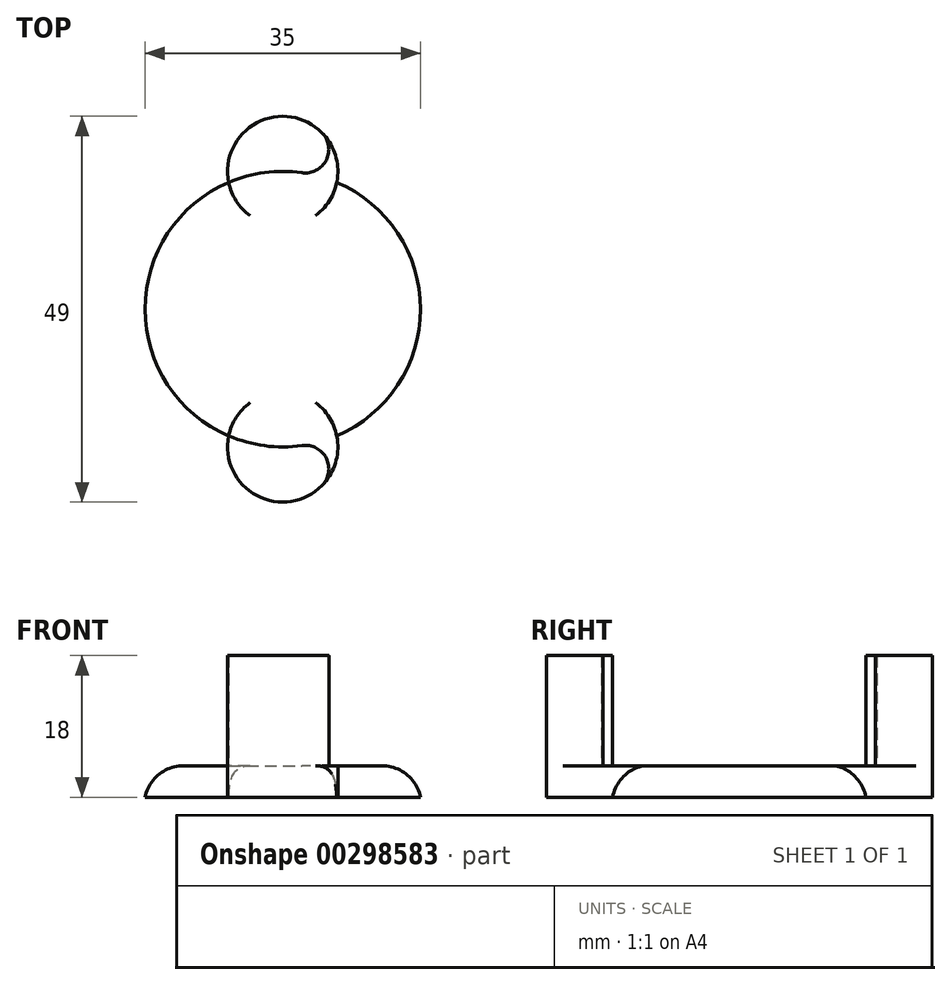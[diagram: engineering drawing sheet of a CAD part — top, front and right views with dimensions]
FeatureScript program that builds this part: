
annotation { "Feature Type Name" : "Feature", "Feature Type Description" : "" }
export const myFeature = defineFeature(function(context is Context, id is Id, definition is map)
    precondition{}
    {
        {
            var Q0;
            Q0=qCreatedBy(makeId("Top.planeOp"),FACE);
            var sketch = newSketch(context, id + "F0", { "sketchPlane" : qUnion([Q0])});
            skCircle(sketch, "E0", {"center": v(0, 0) * mm, "radius": 17.5 * mm});
            skSolve(sketch);
        }
        {
            var Q0;
            Q0 = qSketchRegion(id + "F0", true);
            extrude(context, id + "F1", {"entities" : qUnion([Q0]), "endBound" : BoundingType.SYMMETRIC, "depth" : 4 * mm});
        }
        {
            var Q0;
            Q0=makeQuery(id+"F1.opExtrude","CAP_FACE",FACE,{"disambiguationData":[OSD([sQuery(id+"F0.wireOp",EDGE,"E0")])],"isStart":true});
            var sketch = newSketch(context, id + "F2", { "sketchPlane" : qUnion([Q0])});
            skCircle(sketch, "E1.0.0", {"center": v(0, 0) * mm, "radius": 17.5 * mm});
            skArc(sketch, "E2", {"start": v(-6.86, -16.1) * mm, "mid": v(0, -24.5) * mm, "end": v(6.86, -16.1) * mm});
            skArc(sketch, "E3", {"start": v(6.86, 16.1) * mm, "mid": v(0, 24.5) * mm, "end": v(-6.86, 16.1) * mm});
            skSolve(sketch);
        }
        {
            var Q0;
            {var subQ0=sQuery(id+"F2.wireOp",EDGE,"E3");Q0=makeQuery(id+"F2.imprint","IMPRINT",FACE,{"disambiguationData":[TD([[makeQuery(id+"F2.imprint","IMPRINT",EDGE,{"derivedFrom":subQ0}),1.0]])]});}
            var Q1;
            {var subQ0=sQuery(id+"F2.wireOp",EDGE,"E2");Q1=makeQuery(id+"F2.imprint","IMPRINT",FACE,{"disambiguationData":[TD([[makeQuery(id+"F2.imprint","IMPRINT",EDGE,{"derivedFrom":subQ0}),1.0]])]});}
            extrude(context, id + "F3", {"entities" : qUnion([Q0, Q1]), "operationType" : NewBodyOperationType.ADD, "oppositeDirection" : true, "depth" : 18 * mm});
        }
        {
            var Q0;
            {var subQ0=sQuery(id+"F0.wireOp",EDGE,"E0");var subQ1=sQuery(id+"F2.wireOp",EDGE,"E3");var subQ2=sQuery(id+"F2.wireOp",EDGE,"E1.0.0");Q0=makeQuery(id+"F3.boolean.opBoolean","SPLIT",EDGE,{"disambiguationData":[topologyDisambiguationEdgeConnected([makeQuery(id+"F1.opExtrude","CAP_FACE",FACE,{"disambiguationData":[OSD([subQ0])],"isStart":false}),makeQuery(id+"F3.opExtrude","SWEPT_FACE",FACE,{"disambiguationData":[OSD([subQ2]),TDD([makeQuery(id+"F2.imprint","IMPRINT",EDGE,{"disambiguationData":[TD([[makeQuery(id+"F2.imprint","INTERSECT",VERTEX,{"disambiguationData":[OD(0.0)],"derivedFrom":[subQ2,subQ1]}),1.0]])],"derivedFrom":subQ2})])]})])],"derivedFrom":makeQuery(id+"F1.opExtrude","CAP_EDGE",EDGE,{"disambiguationData":[OSD([subQ0])],"isStart":false})});}
            var Q1;
            {var subQ0=sQuery(id+"F0.wireOp",EDGE,"E0");var subQ1=sQuery(id+"F2.wireOp",EDGE,"E2");var subQ2=sQuery(id+"F2.wireOp",EDGE,"E1.0.0");Q1=makeQuery(id+"F3.boolean.opBoolean","SPLIT",EDGE,{"disambiguationData":[topologyDisambiguationEdgeConnected([makeQuery(id+"F1.opExtrude","CAP_FACE",FACE,{"disambiguationData":[OSD([subQ0])],"isStart":false}),makeQuery(id+"F3.opExtrude","SWEPT_FACE",FACE,{"disambiguationData":[OSD([subQ2]),TDD([makeQuery(id+"F2.imprint","IMPRINT",EDGE,{"disambiguationData":[TD([[makeQuery(id+"F2.imprint","INTERSECT",VERTEX,{"disambiguationData":[OD(0.0)],"derivedFrom":[subQ2,subQ1]}),1.0]])],"derivedFrom":subQ2})])]})])],"derivedFrom":makeQuery(id+"F1.opExtrude","CAP_EDGE",EDGE,{"disambiguationData":[OSD([subQ0])],"isStart":false})});}
            fillet(context, id + "F4", {"entities" : qUnion([Q0, Q1]), "radius" : 5 * mm, "tangentPropagation" : true, "allowEdgeOverflow" : false});
        }
        {
            var Q0;
            {var subQ0=sQuery(id+"F2.wireOp",EDGE,"E3");var subQ1=sQuery(id+"F2.wireOp",EDGE,"E1.0.0");Q0=makeQuery(id+"F3.boolean.opBoolean","SPLIT",EDGE,{"disambiguationData":[topologyDisambiguationEdgeConnected([makeQuery(id+"F1.opExtrude","SWEPT_FACE",FACE,{"disambiguationData":[OSD([sQuery(id+"F0.wireOp",EDGE,"E0")])]})])],"derivedFrom":makeQuery(id+"F3.opExtrude","SWEPT_EDGE",EDGE,{"disambiguationData":[OSD([subQ1,subQ0]),TDD([makeQuery(id+"F2.imprint","INTERSECT",VERTEX,{"disambiguationData":[OD(0.0)],"derivedFrom":[subQ1,subQ0]})])]})});}
            var Q1;
            {var subQ0=sQuery(id+"F2.wireOp",EDGE,"E2");var subQ1=sQuery(id+"F2.wireOp",EDGE,"E1.0.0");Q1=makeQuery(id+"F3.boolean.opBoolean","SPLIT",EDGE,{"disambiguationData":[topologyDisambiguationEdgeConnected([makeQuery(id+"F1.opExtrude","SWEPT_FACE",FACE,{"disambiguationData":[OSD([sQuery(id+"F0.wireOp",EDGE,"E0")])]})])],"derivedFrom":makeQuery(id+"F3.opExtrude","SWEPT_EDGE",EDGE,{"disambiguationData":[OSD([subQ1,subQ0]),TDD([makeQuery(id+"F2.imprint","INTERSECT",VERTEX,{"disambiguationData":[OD(1.0)],"derivedFrom":[subQ1,subQ0]})])]})});}
            var Q2;
            {var subQ0=sQuery(id+"F2.wireOp",EDGE,"E2");var subQ1=sQuery(id+"F2.wireOp",EDGE,"E1.0.0");Q2=makeQuery(id+"F3.boolean.opBoolean","SPLIT",EDGE,{"disambiguationData":[topologyDisambiguationEdgeConnected([makeQuery(id+"F1.opExtrude","SWEPT_FACE",FACE,{"disambiguationData":[OSD([sQuery(id+"F0.wireOp",EDGE,"E0")])]})])],"derivedFrom":makeQuery(id+"F3.opExtrude","SWEPT_EDGE",EDGE,{"disambiguationData":[OSD([subQ1,subQ0]),TDD([makeQuery(id+"F2.imprint","INTERSECT",VERTEX,{"disambiguationData":[OD(0.0)],"derivedFrom":[subQ1,subQ0]})])]})});}
            var Q3;
            {var subQ0=sQuery(id+"F2.wireOp",EDGE,"E3");var subQ1=sQuery(id+"F2.wireOp",EDGE,"E1.0.0");Q3=makeQuery(id+"F3.boolean.opBoolean","SPLIT",EDGE,{"disambiguationData":[topologyDisambiguationEdgeConnected([makeQuery(id+"F1.opExtrude","SWEPT_FACE",FACE,{"disambiguationData":[OSD([sQuery(id+"F0.wireOp",EDGE,"E0")])]})])],"derivedFrom":makeQuery(id+"F3.opExtrude","SWEPT_EDGE",EDGE,{"disambiguationData":[OSD([subQ1,subQ0]),TDD([makeQuery(id+"F2.imprint","INTERSECT",VERTEX,{"disambiguationData":[OD(1.0)],"derivedFrom":[subQ1,subQ0]})])]})});}
            fillet(context, id + "F5", {"entities" : qUnion([Q0, Q1, Q2, Q3]), "radius" : 3 * mm, "tangentPropagation" : true, "allowEdgeOverflow" : false});
        }
    });
